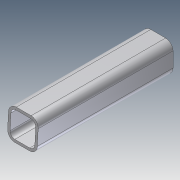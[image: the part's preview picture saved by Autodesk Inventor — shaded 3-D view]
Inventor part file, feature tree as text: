
AUTODESK INVENTOR PART (.ipt)
format: ipt  version: unknown  size: 194,560 bytes
history: native  units: in
note: dims shown in document units (in); Inventor stores cm internally (conversion verified against a paired STEP export)
features: extrude x2, sketch x2
ambient origin geometry x8: Origin, YZ Plane, XZ Plane, XY Plane, X Axis, Y Axis, Z Axis, Center Point
bodies: Solid1 (feature_tree)
feature tree (4):
  extrude  "Extrusion1"  Depth=0.375in
  extrude  "Extrusion2"  Depth=6.875in TaperAngle=0.0deg
  sketch  "Sketch1"  dims[d0=1.5in d1=0.375in]
  sketch  "Sketch2"  dims[d2=0.125in d3=6.875in d4=0.0in d5=0.0206in d6=7.0in d7=0.0in]
